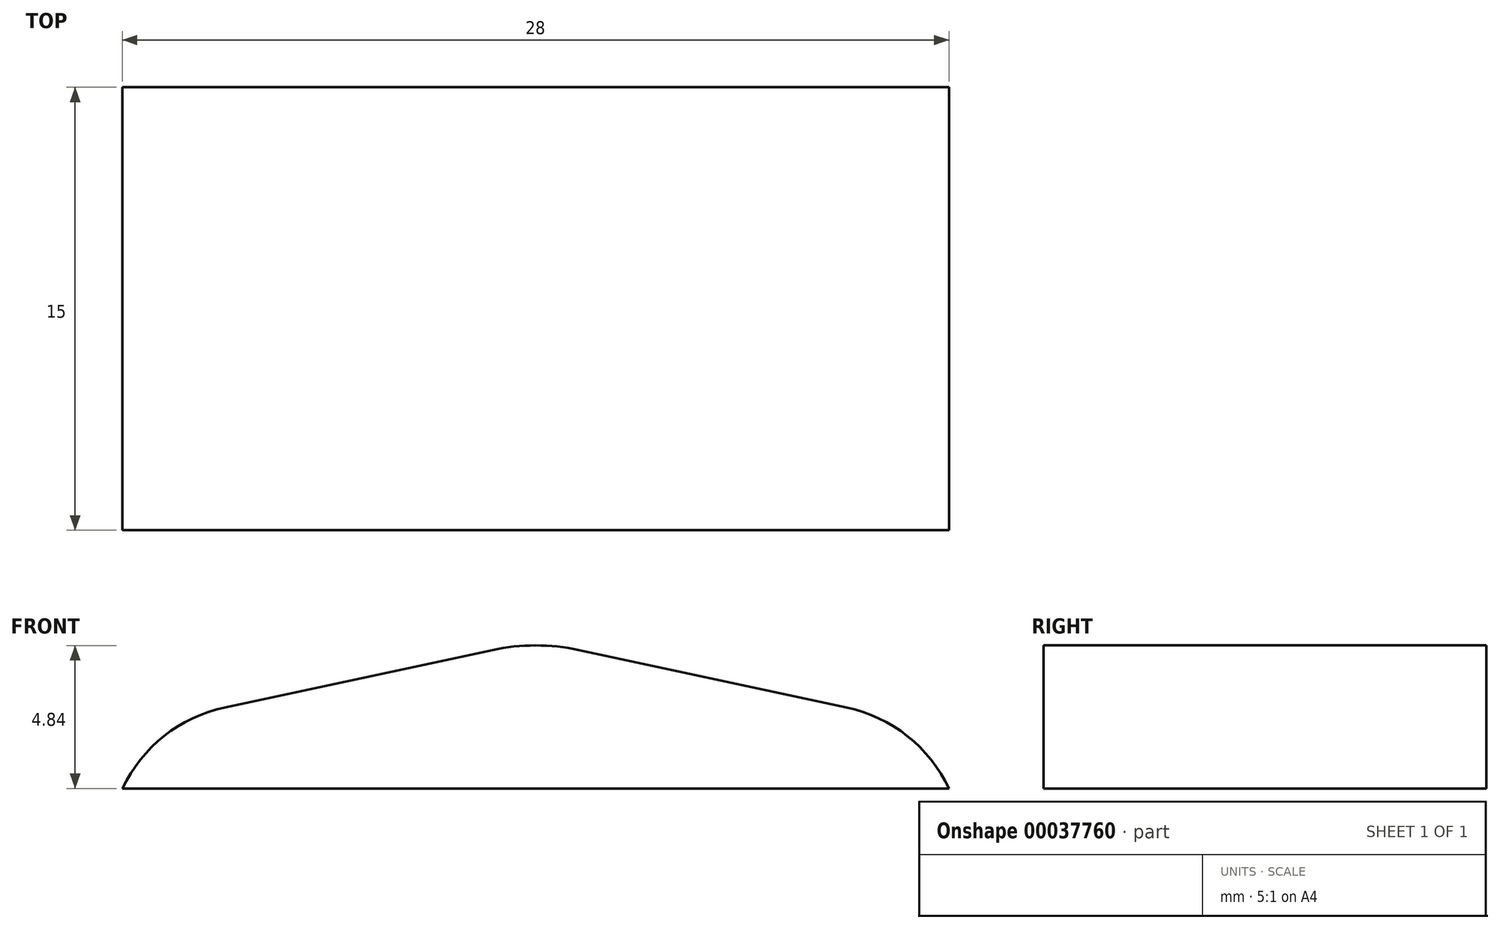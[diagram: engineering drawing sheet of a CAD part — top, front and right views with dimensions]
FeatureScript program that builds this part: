
annotation { "Feature Type Name" : "Feature", "Feature Type Description" : "" }
export const myFeature = defineFeature(function(context is Context, id is Id, definition is map)
    precondition{}
    {
        {
            var Q0;
            Q0=qCreatedBy(makeId("Front.planeOp"),FACE);
            var sketch = newSketch(context, id + "F0", { "sketchPlane" : qUnion([Q0])});
            skLineSegment(sketch, "E0", {"start": v(14, 0) * mm, "end": v(-14, 0) * mm});
            skLineSegment(sketch, "E1", {"start": v(-14, 0) * mm, "end": v(-14, 2) * mm});
            skLineSegment(sketch, "E2", {"start": v(-14, 2) * mm, "end": v(0, 5) * mm});
            skLineSegment(sketch, "E3", {"start": v(0, 5) * mm, "end": v(14, 2) * mm});
            skLineSegment(sketch, "E4", {"start": v(14, 2) * mm, "end": v(14, 0) * mm});
            skSolve(sketch);
        }
        {
            var Q0;
            Q0 = qSketchRegion(id + "F0", true);
            extrude(context, id + "F1", {"entities" : qUnion([Q0]), "depth" : 15 * mm});
        }
        {
            var Q0;
            Q0=makeQuery(id+"F1.opExtrude","SWEPT_EDGE",EDGE,{"disambiguationData":[OSD([sQuery(id+"F0.wireOp",EDGE,"E1"),sQuery(id+"F0.wireOp",EDGE,"E2")])]});
            var Q1;
            Q1=makeQuery(id+"F1.opExtrude","SWEPT_EDGE",EDGE,{"disambiguationData":[OSD([sQuery(id+"F0.wireOp",EDGE,"E3"),sQuery(id+"F0.wireOp",EDGE,"E4")])]});
            fillet(context, id + "F2", {"entities" : qUnion([Q0, Q1]), "radius" : 5 * mm, "tangentPropagation" : true, "allowEdgeOverflow" : false});
        }
        {
            var Q0;
            Q0=makeQuery(id+"F1.opExtrude","SWEPT_EDGE",EDGE,{"disambiguationData":[OSD([sQuery(id+"F0.wireOp",EDGE,"E2"),sQuery(id+"F0.wireOp",EDGE,"E3")])]});
            fillet(context, id + "F3", {"entities" : qUnion([Q0]), "radius" : 7 * mm, "tangentPropagation" : true, "allowEdgeOverflow" : false});
        }
    });
